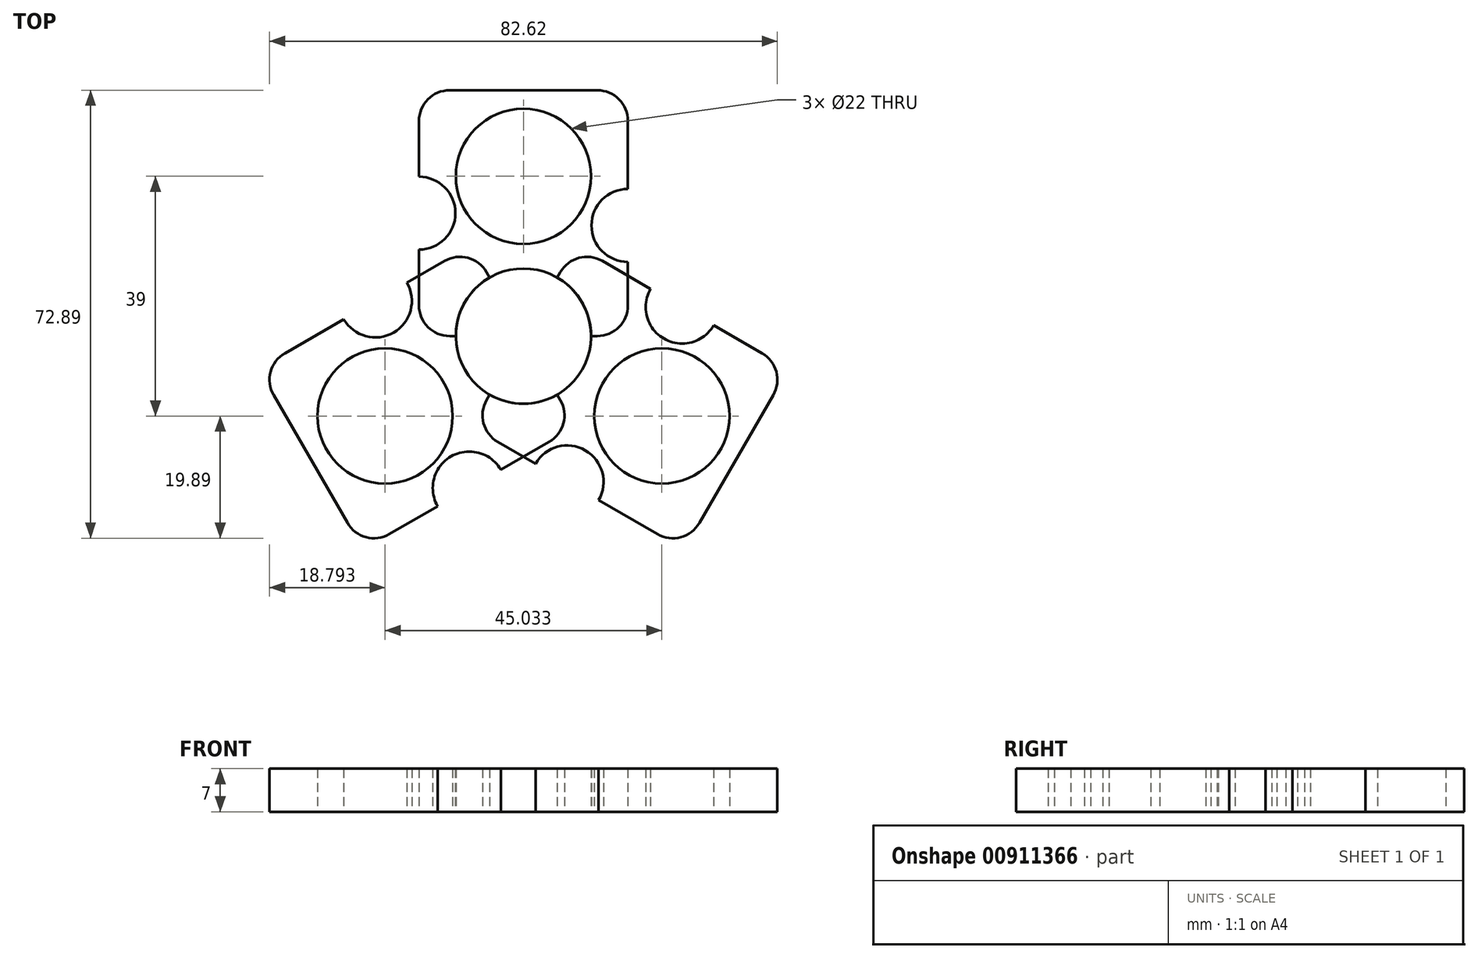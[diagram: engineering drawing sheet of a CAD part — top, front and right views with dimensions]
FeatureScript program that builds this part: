
annotation { "Feature Type Name" : "Feature", "Feature Type Description" : "" }
export const myFeature = defineFeature(function(context is Context, id is Id, definition is map)
    precondition{}
    {
        {
            var Q0;
            Q0=qCreatedBy(makeId("Top.planeOp"),FACE);
            var sketch = newSketch(context, id + "F0", { "sketchPlane" : qUnion([Q0])});
            skCircle(sketch, "E0", {"center": v(0, 0) * mm, "radius": 11 * mm});
            skLineSegment(sketch, "E1.bottom", {"start": v(0, 0) * mm, "end": v(12, 0) * mm});
            skLineSegment(sketch, "E1.top", {"start": v(0, 40) * mm, "end": v(12, 40) * mm});
            skLineSegment(sketch, "E1.left", {"start": v(0, 0) * mm, "end": v(0, 40) * mm});
            skLineSegment(sketch, "E1.right", {"start": v(17, 5) * mm, "end": v(17, 35) * mm});
            skLineSegment(sketch, "E2.bottom", {"start": v(0, 0) * mm, "end": v(-12, 0) * mm});
            skLineSegment(sketch, "E2.top", {"start": v(0, 40) * mm, "end": v(-12, 40) * mm});
            skLineSegment(sketch, "E2.right", {"start": v(-17, 5) * mm, "end": v(-17, 35) * mm});
            skLineSegment(sketch, "E3", {"start": v(0, 40) * mm, "end": v(0, 26) * mm});
            skCircle(sketch, "E4", {"center": v(0, 26) * mm, "radius": 11 * mm});
            skPoint(sketch, "E5.visualSharp", {"position": v(-17, 0) * mm});
            skArc(sketch, "E5.filletArc", {"start": v(-17, 5) * mm, "mid": v(-15.54, 1.46) * mm, "end": v(-12, 0) * mm});
            skPoint(sketch, "E6.visualSharp", {"position": v(-17, 40) * mm});
            skArc(sketch, "E6.filletArc", {"start": v(-12, 40) * mm, "mid": v(-15.54, 38.54) * mm, "end": v(-17, 35) * mm});
            skPoint(sketch, "E7.visualSharp", {"position": v(17, 40) * mm});
            skArc(sketch, "E7.filletArc", {"start": v(17, 35) * mm, "mid": v(15.54, 38.54) * mm, "end": v(12, 40) * mm});
            skPoint(sketch, "E8.visualSharp", {"position": v(17, 0) * mm});
            skArc(sketch, "E8.filletArc", {"start": v(12, 0) * mm, "mid": v(15.54, 1.46) * mm, "end": v(17, 5) * mm});
            skCircle(sketch, "E9", {"center": v(-17, 20) * mm, "radius": 5.93 * mm});
            skCircle(sketch, "E10", {"center": v(17, 18) * mm, "radius": 5.93 * mm});
            skSolve(sketch);
        }
        {
            var Q0;
            {var subQ0=sQuery(id+"F0.wireOp",EDGE,"E2.top");Q0=makeQuery(id+"F0.imprint","IMPRINT",FACE,{"disambiguationData":[TD([[makeQuery(id+"F0.imprint","IMPRINT",EDGE,{"derivedFrom":subQ0}),1.0]])]});}
            var Q1;
            {var subQ9=sQuery(id+"F0.wireOp",EDGE,"E1.top");Q1=makeQuery(id+"F0.imprint","IMPRINT",FACE,{"disambiguationData":[TD([[makeQuery(id+"F0.imprint","IMPRINT",EDGE,{"derivedFrom":subQ9}),-1.0]])]});}
            extrude(context, id + "F1", {"entities" : qUnion([Q0, Q1]), "depth" : 7 * mm, "offsetDistance" : 25 * mm});
        }
        {
            var Q0;
            Q0=qCreatedBy(makeId("Front.planeOp"),FACE);
            var sketch = newSketch(context, id + "F2", { "sketchPlane" : qUnion([Q0])});
            skLineSegment(sketch, "E11", {"start": v(0, 0) * mm, "end": v(0, 56.76) * mm});
            skSolve(sketch);
        }
        {
            var Q0;
            Q0=makeQuery(id+"F1.opExtrude","SWEPT_BODY",BODY,{"disambiguationData":[OSD([sQuery(id+"F0.wireOp",EDGE,"E0"),sQuery(id+"F0.wireOp",EDGE,"E1.bottom"),sQuery(id+"F0.wireOp",EDGE,"E1.top"),sQuery(id+"F0.wireOp",EDGE,"E1.right"),sQuery(id+"F0.wireOp",EDGE,"E2.bottom"),sQuery(id+"F0.wireOp",EDGE,"E2.top"),sQuery(id+"F0.wireOp",EDGE,"E2.right"),sQuery(id+"F0.wireOp",EDGE,"E4")])]});
            var Q1;
            Q1=sQuery(id+"F2.wireOp",EDGE,"E11");
            transform(context, id + "F3", {"entities" : qUnion([Q0]), "transformType" : TransformType.ROTATION, "transformAxis" : qUnion([Q1]), "angle" : 120 * degree, "makeCopy" : true});
        }
        {
            var Q0;
            Q0=makeQuery(id+"F1.opExtrude","SWEPT_BODY",BODY,{"disambiguationData":[OSD([sQuery(id+"F0.wireOp",EDGE,"E0"),sQuery(id+"F0.wireOp",EDGE,"E1.bottom"),sQuery(id+"F0.wireOp",EDGE,"E1.top"),sQuery(id+"F0.wireOp",EDGE,"E1.right"),sQuery(id+"F0.wireOp",EDGE,"E2.bottom"),sQuery(id+"F0.wireOp",EDGE,"E2.top"),sQuery(id+"F0.wireOp",EDGE,"E2.right"),sQuery(id+"F0.wireOp",EDGE,"E4")])]});
            var Q1;
            Q1=sQuery(id+"F2.wireOp",EDGE,"E11");
            transform(context, id + "F4", {"entities" : qUnion([Q0]), "transformType" : TransformType.ROTATION, "transformAxis" : qUnion([Q1]), "angle" : 240 * degree, "makeCopy" : true});
        }
    });
